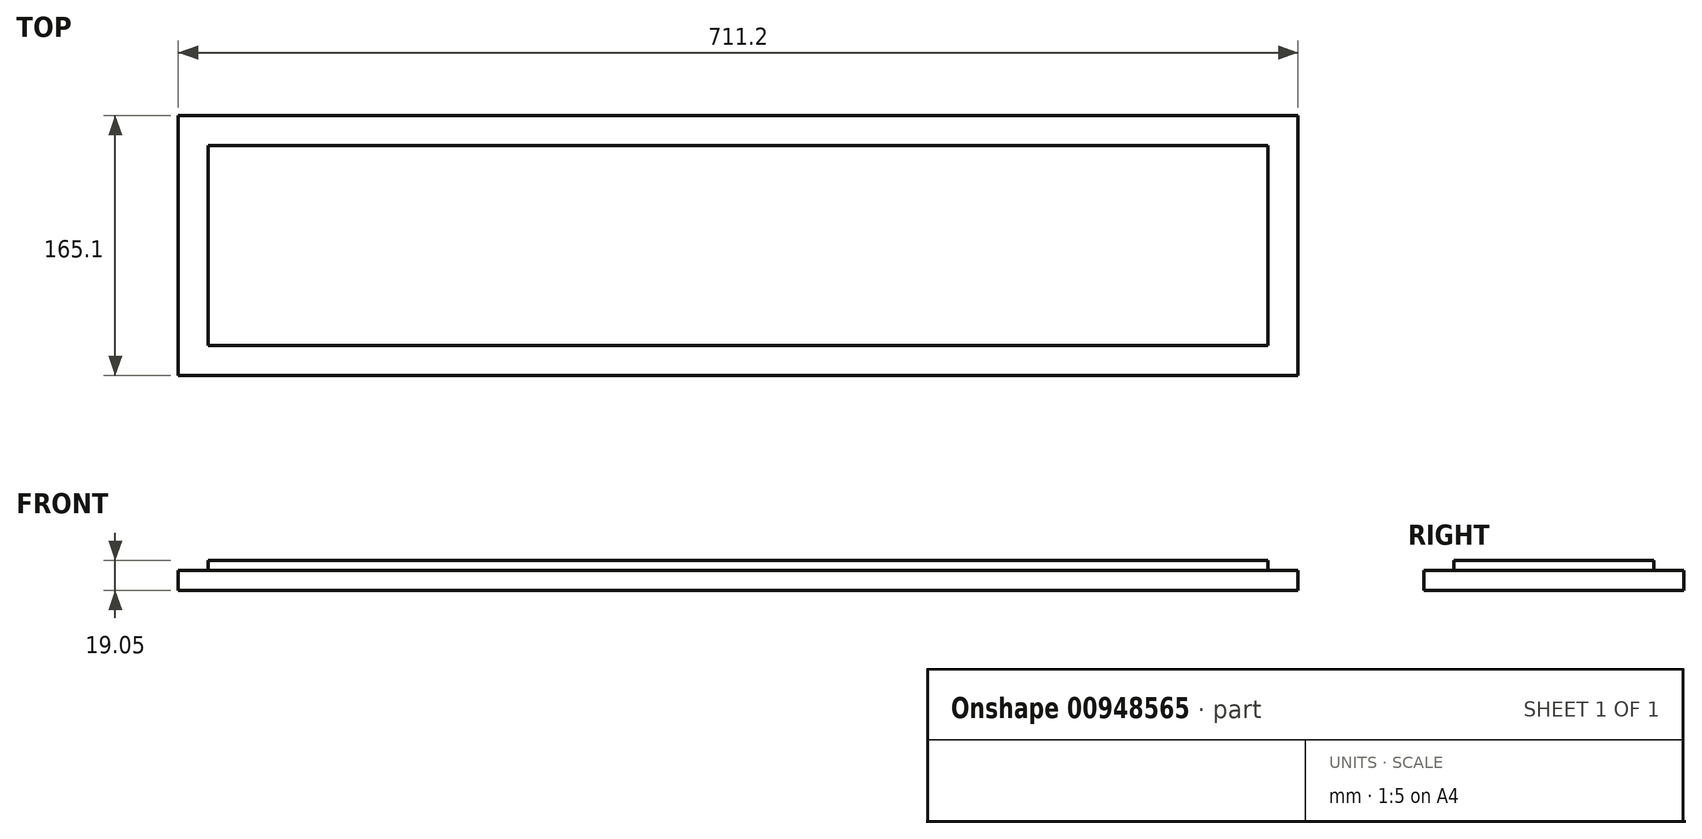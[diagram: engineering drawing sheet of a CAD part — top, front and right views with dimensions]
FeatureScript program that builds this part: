
annotation { "Feature Type Name" : "Feature", "Feature Type Description" : "" }
export const myFeature = defineFeature(function(context is Context, id is Id, definition is map)
    precondition{}
    {
        {
            var Q0;
            Q0=qCreatedBy(makeId("Top.planeOp"),FACE);
            var sketch = newSketch(context, id + "F0", { "sketchPlane" : qUnion([Q0])});
            skLineSegment(sketch, "E0.bottom", {"start": v(355.6, -82.55) * mm, "end": v(-355.6, -82.55) * mm});
            skLineSegment(sketch, "E0.top", {"start": v(355.6, 82.55) * mm, "end": v(-355.6, 82.55) * mm});
            skLineSegment(sketch, "E0.left", {"start": v(355.6, -82.55) * mm, "end": v(355.6, 82.55) * mm});
            skLineSegment(sketch, "E0.right", {"start": v(-355.6, -82.55) * mm, "end": v(-355.6, 82.55) * mm});
            skPoint(sketch, "E0.middle", {"position": v(0, 0) * mm});
            skSolve(sketch);
        }
        {
            var Q0;
            Q0=makeQuery(id+"F0.imprint","IMPRINT",FACE,{"disambiguationData":[TD([[makeQuery(id+"F0.imprint","IMPRINT",EDGE,{"derivedFrom":sQuery(id+"F0.wireOp",EDGE,"E0.bottom")}),-1.0]])]});
            extrude(context, id + "F1", {"entities" : qUnion([Q0]), "depth" : 19.05 * mm, "offsetDistance" : 25.4 * mm});
        }
        {
            var Q0;
            Q0=makeQuery(id+"F1.opExtrude","CAP_FACE",FACE,{"disambiguationData":[OSD([sQuery(id+"F0.wireOp",EDGE,"E0.bottom"),sQuery(id+"F0.wireOp",EDGE,"E0.top"),sQuery(id+"F0.wireOp",EDGE,"E0.left"),sQuery(id+"F0.wireOp",EDGE,"E0.right")])],"isStart":false});
            var sketch = newSketch(context, id + "F2", { "sketchPlane" : qUnion([Q0])});
            skLineSegment(sketch, "E1.bottom", {"start": v(-355.6, -82.55) * mm, "end": v(-336.55, -82.55) * mm});
            skLineSegment(sketch, "E1.top", {"start": v(-355.6, 82.55) * mm, "end": v(-336.55, 82.55) * mm});
            skLineSegment(sketch, "E1.left", {"start": v(-355.6, -82.55) * mm, "end": v(-355.6, 82.55) * mm});
            skLineSegment(sketch, "E1.right", {"start": v(-336.55, -82.55) * mm, "end": v(-336.55, 82.55) * mm});
            skLineSegment(sketch, "E2.bottom", {"start": v(355.6, -82.55) * mm, "end": v(336.55, -82.55) * mm});
            skLineSegment(sketch, "E2.top", {"start": v(355.6, 82.55) * mm, "end": v(336.55, 82.55) * mm});
            skLineSegment(sketch, "E2.left", {"start": v(355.6, -82.55) * mm, "end": v(355.6, 82.55) * mm});
            skLineSegment(sketch, "E2.right", {"start": v(336.55, -82.55) * mm, "end": v(336.55, 82.55) * mm});
            skLineSegment(sketch, "E3.bottom", {"start": v(-355.6, -82.55) * mm, "end": v(355.6, -82.55) * mm});
            skLineSegment(sketch, "E3.top", {"start": v(-355.6, -63.5) * mm, "end": v(355.6, -63.5) * mm});
            skLineSegment(sketch, "E3.left", {"start": v(-355.6, -82.55) * mm, "end": v(-355.6, -63.5) * mm});
            skLineSegment(sketch, "E3.right", {"start": v(355.6, -82.55) * mm, "end": v(355.6, -63.5) * mm});
            skLineSegment(sketch, "E4.bottom", {"start": v(-355.6, 82.55) * mm, "end": v(355.6, 82.55) * mm});
            skLineSegment(sketch, "E4.top", {"start": v(-355.6, 63.5) * mm, "end": v(355.6, 63.5) * mm});
            skLineSegment(sketch, "E4.left", {"start": v(-355.6, 82.55) * mm, "end": v(-355.6, 63.5) * mm});
            skLineSegment(sketch, "E4.right", {"start": v(355.6, 82.55) * mm, "end": v(355.6, 63.5) * mm});
            skSolve(sketch);
        }
        {
            var Q0;
            {var subQ0=sQuery(id+"F2.wireOp",EDGE,"E3.bottom");var subQ1=sQuery(id+"F2.wireOp",EDGE,"E1.right");var subQ2=makeQuery(id+"F2.imprint","INTERSECT",VERTEX,{"derivedFrom":[subQ1,subQ0]});Q0=makeQuery(id+"F2.imprint","IMPRINT",FACE,{"disambiguationData":[TD([[makeQuery(id+"F2.imprint","IMPRINT",EDGE,{"disambiguationData":[TD([[subQ2,-1.0]])],"derivedFrom":subQ1}),-1.0]])]});}
            var Q1;
            {var subQ5=sQuery(id+"F2.wireOp",EDGE,"E3.left");Q1=makeQuery(id+"F2.imprint","IMPRINT",FACE,{"disambiguationData":[TD([[makeQuery(id+"F2.imprint","IMPRINT",EDGE,{"derivedFrom":subQ5}),-1.0]])]});}
            var Q2;
            {var subQ0=sQuery(id+"F2.wireOp",EDGE,"E1.top");Q2=makeQuery(id+"F2.imprint","IMPRINT",FACE,{"disambiguationData":[TD([[makeQuery(id+"F2.imprint","IMPRINT",EDGE,{"derivedFrom":subQ0}),1.0]])]});}
            var Q3;
            {var subQ5=sQuery(id+"F2.wireOp",EDGE,"E3.right");Q3=makeQuery(id+"F2.imprint","IMPRINT",FACE,{"disambiguationData":[TD([[makeQuery(id+"F2.imprint","IMPRINT",EDGE,{"derivedFrom":subQ5}),1.0]])]});}
            var Q4;
            {var subQ0=sQuery(id+"F2.wireOp",EDGE,"E2.top");Q4=makeQuery(id+"F2.imprint","IMPRINT",FACE,{"disambiguationData":[TD([[makeQuery(id+"F2.imprint","IMPRINT",EDGE,{"derivedFrom":subQ0}),1.0]])]});}
            var Q5;
            {var subQ5=sQuery(id+"F2.wireOp",EDGE,"E4.left");Q5=makeQuery(id+"F2.imprint","IMPRINT",FACE,{"disambiguationData":[TD([[makeQuery(id+"F2.imprint","IMPRINT",EDGE,{"derivedFrom":subQ5}),-1.0]])]});}
            var Q6;
            {var subQ0=sQuery(id+"F2.wireOp",EDGE,"E4.bottom");var subQ1=sQuery(id+"F2.wireOp",EDGE,"E1.right");var subQ2=makeQuery(id+"F2.imprint","INTERSECT",VERTEX,{"derivedFrom":[subQ1,subQ0]});Q6=makeQuery(id+"F2.imprint","IMPRINT",FACE,{"disambiguationData":[TD([[makeQuery(id+"F2.imprint","IMPRINT",EDGE,{"disambiguationData":[TD([[subQ2,1.0]])],"derivedFrom":subQ1}),-1.0]])]});}
            var Q7;
            {var subQ5=sQuery(id+"F2.wireOp",EDGE,"E4.right");Q7=makeQuery(id+"F2.imprint","IMPRINT",FACE,{"disambiguationData":[TD([[makeQuery(id+"F2.imprint","IMPRINT",EDGE,{"derivedFrom":subQ5}),1.0]])]});}
            var Q8;
            {var subQ0=sQuery(id+"F2.wireOp",EDGE,"E1.left");Q8=makeQuery(id+"F2.imprint","IMPRINT",FACE,{"disambiguationData":[TD([[makeQuery(id+"F2.imprint","IMPRINT",EDGE,{"derivedFrom":subQ0}),-1.0]])]});}
            var Q9;
            {var subQ0=sQuery(id+"F2.wireOp",EDGE,"E2.left");Q9=makeQuery(id+"F2.imprint","IMPRINT",FACE,{"disambiguationData":[TD([[makeQuery(id+"F2.imprint","IMPRINT",EDGE,{"derivedFrom":subQ0}),1.0]])]});}
            extrude(context, id + "F3", {"entities" : qUnion([Q0, Q1, Q2, Q3, Q4, Q5, Q6, Q7, Q8, Q9]), "operationType" : NewBodyOperationType.REMOVE, "oppositeDirection" : true, "depth" : 6.35 * mm, "offsetDistance" : 25.4 * mm});
        }
    });
